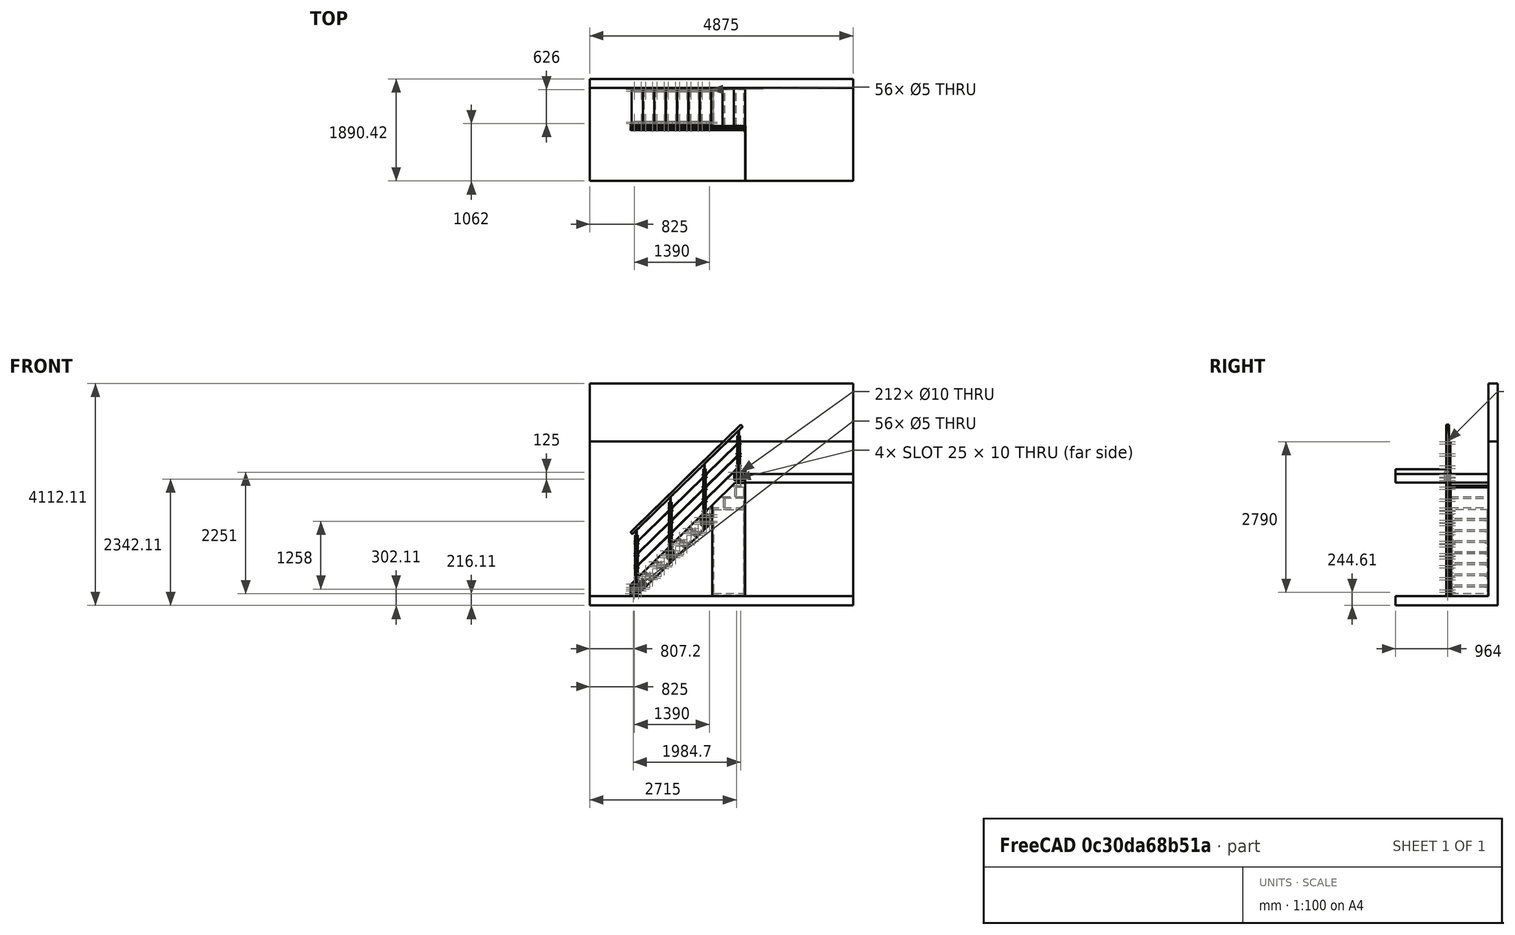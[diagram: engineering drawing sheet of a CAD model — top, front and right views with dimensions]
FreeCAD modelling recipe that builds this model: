
FCSTD DOCUMENT  (FreeCAD 0.17R11051 (Git))
Label: railing_last_element_rear
License: All rights reserved
LicenseURL: http://en.wikipedia.org/wiki/All_rights_reserved
objects: Part::FeaturePython×23, Part::Compound×2, TechDraw::DrawSVGTemplate×1, Part::Part2DObjectPython×1, Part::Extrusion×1, Part::Cut×1, App::DocumentObjectGroup×1, TechDraw::DrawViewMulti×1, TechDraw::DrawPage×1
note: 28 computed .brp shape members not serialized (recipe doc carries the construction recipe); baked Part::Feature solids carry a one-line shape summary decoded from their .brp

FEATURE [Part::FeaturePython] double_beam_01  # a2plus imported part (geometry in sourceFile) (typed FeaturePython)
  fixedPosition = true
  sourceFile = double_beam.fcstd
  timeLastImport = 1.49424e+09
  updateColors = true
FEATURE [Part::FeaturePython] fasteners_01  # a2plus imported part (geometry in sourceFile) (typed FeaturePython)
  fixedPosition = false
  sourceFile = fasteners.fcstd
  timeLastImport = 1.49442e+09
  updateColors = true
FEATURE [Part::FeaturePython] railing_plate_01  # a2plus imported part (geometry in sourceFile) (typed FeaturePython)
  fixedPosition = false
  sourceFile = railing_plate.fcstd
  timeLastImport = 1.49443e+09
  updateColors = true
FEATURE [Part::FeaturePython] railing_dist_01  # a2plus imported part (geometry in sourceFile) (typed FeaturePython)
  fixedPosition = false
  sourceFile = railing_dist.fcstd
  timeLastImport = 1.49443e+09
  updateColors = true
FEATURE [Part::FeaturePython] railing_eyelet_01  # a2plus imported part (geometry in sourceFile) (typed FeaturePython)
  fixedPosition = false
  sourceFile = railing_eyelet.fcstd
  timeLastImport = 1.49443e+09
  updateColors = true
FEATURE [Part::FeaturePython] railing_fasteners_01  # a2plus imported part (geometry in sourceFile) (typed FeaturePython)
  fixedPosition = false
  sourceFile = railing_fasteners.fcstd
  timeLastImport = 1.49443e+09
  updateColors = true
FEATURE [Part::FeaturePython] ropes_01  # a2plus imported part (geometry in sourceFile) (typed FeaturePython)
  fixedPosition = false
  sourceFile = ropes.fcstd
  timeLastImport = 1.49443e+09
  updateColors = true
FEATURE [Part::FeaturePython] step_01  # a2plus imported part (geometry in sourceFile) (typed FeaturePython)
  fixedPosition = false
  sourceFile = step.fcstd
  timeLastImport = 1.49443e+09
  updateColors = true
FEATURE [Part::FeaturePython] handrail_holder_01  # a2plus imported part (geometry in sourceFile) (typed FeaturePython)
  fixedPosition = false
  sourceFile = handrail_holder.fcstd
  timeLastImport = 1.49443e+09
  updateColors = true
FEATURE [Part::FeaturePython] handrail_01  # a2plus imported part (geometry in sourceFile) (typed FeaturePython)
  Placement = pos=(-318.108,494.458,1490.85) rot=(0,1,0;3.93904rad)
  fixedPosition = false
  sourceFile = handrail.fcstd
  timeLastImport = 1.49444e+09
  updateColors = true
FEATURE [Part::FeaturePython] Array001  label="ropes"  # Draft array (typed FeaturePython)
  Angle = 360
  ArrayType = 0
  Axis = (0,0,1)
  Base = -> ropes_01
  Center = (0,0,0)
  Fuse = false
  IntervalAxis = (0,0,0)
  IntervalX = (630,0,615)
  IntervalY = (0,1,0)
  IntervalZ = (0,0,0)
  NumberPolar = 1
  NumberX = 3
  NumberY = 1
  NumberZ = 1
FEATURE [Part::FeaturePython] railing_wood_01  # a2plus imported part (geometry in sourceFile) (typed FeaturePython)
  fixedPosition = false
  sourceFile = railing_wood.fcstd
  timeLastImport = 1.49443e+09
  updateColors = true
FEATURE [Part::Compound] Compound
  Links = -> [railing_plate_01,handrail_holder_01,railing_fasteners_01,railing_eyelet_01,railing_dist_01,railing_wood_01]
FEATURE [Part::FeaturePython] Array  # Draft array (typed FeaturePython)
  Angle = 360
  ArrayType = 0
  Axis = (0,0,1)
  Base = -> Compound
  Center = (0,0,0)
  Fuse = false
  IntervalAxis = (0,0,0)
  IntervalX = (630,0,615)
  IntervalY = (0,1,0)
  IntervalZ = (0,0,0)
  NumberPolar = 1
  NumberX = 3
  NumberY = 1
  NumberZ = 1
FEATURE [Part::FeaturePython] fridge_box_panels_01  # a2plus imported part (geometry in sourceFile) (typed FeaturePython)
  fixedPosition = false
  sourceFile = fridge_box_panels.fcstd
  timeLastImport = 1.49389e+09
  updateColors = true
FEATURE [Part::FeaturePython] fridge_box_door_01  # a2plus imported part (geometry in sourceFile) (typed FeaturePython)
  fixedPosition = false
  sourceFile = fridge_box_door.fcstd
  timeLastImport = 1.49385e+09
  updateColors = true
FEATURE [Part::FeaturePython] handrail_holder_002  # a2plus imported part (geometry in sourceFile) (typed FeaturePython)
  Placement = pos=(1890,0,1845) rot=(0,0,1;0rad)
  fixedPosition = false
  sourceFile = handrail_holder.fcstd
  timeLastImport = 1.49443e+09
  updateColors = true
FEATURE [Part::FeaturePython] railing_eyelet_002  # a2plus imported part (geometry in sourceFile) (typed FeaturePython)
  Placement = pos=(1890,0,1845) rot=(0,0,1;0rad)
  fixedPosition = false
  sourceFile = railing_eyelet.fcstd
  timeLastImport = 1.49443e+09
  updateColors = true
FEATURE [Part::FeaturePython] railing_last_wood_01  # a2plus imported part (geometry in sourceFile) (typed FeaturePython)
  Placement = pos=(1890,0,1845) rot=(0,0,1;0rad)
  fixedPosition = false
  sourceFile = railing_last_wood.fcstd
  timeLastImport = 1.49443e+09
  updateColors = true
FEATURE [Part::FeaturePython] stair_profile_01  # a2plus imported part (geometry in sourceFile) (typed FeaturePython)
  fixedPosition = false
  sourceFile = stair_profile.fcstd
  timeLastImport = 1.4938e+09
  updateColors = true
FEATURE [Part::FeaturePython] room_01  # a2plus imported part (geometry in sourceFile) (typed FeaturePython)
  fixedPosition = false
  sourceFile = room.fcstd
  timeLastImport = 1.49444e+09
  updateColors = true
FEATURE [Part::FeaturePython] plate_01  # a2plus imported part (geometry in sourceFile) (typed FeaturePython)
  fixedPosition = false
  sourceFile = plate.fcstd
  timeLastImport = 1.49399e+09
  updateColors = true
FEATURE [TechDraw::DrawSVGTemplate] Template
  Height = 841
  Orientation = 0
  Width = 594
FEATURE [Part::Part2DObjectPython] Rectangle  # Draft 2D object (typed FeaturePython)
  ChamferSize = 0
  Columns = 1
  FilletRadius = 0
  Height = 1074.89
  Length = 4875
  MakeFace = true
  Placement = pos=(-775,345,2865.11) rot=(1,0,0;1.5708rad)
  Rows = 1
  Support = -> [room_01]
FEATURE [Part::Extrusion] Extrude
  Base = -> Rectangle
  Dir = (0,1,0)
  DirMode = 0
  FaceMakerClass = Part::FaceMakerBullseye
  LengthFwd = 500
  LengthRev = 0
  Solid = false
  Symmetric = false
FEATURE [Part::Cut] Cut  label="Cutted_room"
  Base = -> room_01
  Tool = -> Extrude
FEATURE [Part::FeaturePython] room_002  # a2plus imported part (geometry in sourceFile) (typed FeaturePython)
  fixedPosition = false
  sourceFile = room.fcstd
  timeLastImport = 1.49444e+09
  updateColors = true
FEATURE [App::DocumentObjectGroup] Group  label="ref"
  Group = -> [double_beam_01,fasteners_01,step_01,Array001,fridge_box_panels_01,fridge_box_door_01,stair_profile_01,plate_01,Cut,room_002]
FEATURE [Part::FeaturePython] railing_last_steel_02  # a2plus imported part (geometry in sourceFile) (typed FeaturePython)
  Placement = pos=(1890,0,2070) rot=(0,0,1;0rad)
  fixedPosition = false
  sourceFile = railing_last_steel.fcstd
  timeLastImport = 1.49451e+09
  updateColors = true
FEATURE [Part::Compound] Compound001  label="last_railing"
  Links = -> [handrail_holder_002,railing_eyelet_002,railing_last_wood_01,railing_last_steel_02]
FEATURE [TechDraw::DrawViewMulti] MultiView
  ArcCenterMarks = true
  CenterScale = 2
  Direction = (-1,1,1.5)
  HardHidden = true
  HiddenWidth = 0.15
  HorizCenterLine = false
  IsoCount = 0
  IsoHidden = false
  IsoVisible = false
  IsoWidth = 0.3
  KeepLabel = false
  LineWidth = 0.2
  Rotation = 0
  Scale = 0.1
  ScaleType = 2
  SeamHidden = false
  SeamVisible = false
  ShowSectionLine = true
  SmoothHidden = false
  SmoothVisible = false
  Source = -> Cut
  Sources = -> [Cut,fridge_box_panels_01,fridge_box_door_01,Array001,handrail_01,Compound001]
  VertCenterLine = false
  X = 272.911
  Y = 346.547
FEATURE [TechDraw::DrawPage] Page
  ProjectionType = 0
  Template = -> Template
  Views = -> [MultiView]
